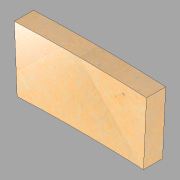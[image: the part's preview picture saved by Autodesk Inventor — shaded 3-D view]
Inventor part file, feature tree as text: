
AUTODESK INVENTOR PART (.ipt)
format: ipt  version: 2022.1 (Build 261234020, 234B)  size: 115,712 bytes
history: imported  units: in
note: dims shown in document units (in); Inventor stores cm internally (conversion verified against a paired STEP export)
features: imported_body x1
ambient origin geometry x8: Origin, YZ Plane, XZ Plane, XY Plane, X Axis, Y Axis, Z Axis, Center Point
bodies: Solid1 (imported_parasolid), Body1 (imported_parasolid)
feature tree (1):
  imported_body  NMx_Import_Brep_tag  [imported B-rep: ~6 faces, bbox_mm=[1053.068993, 509.28941, 152.4]]
